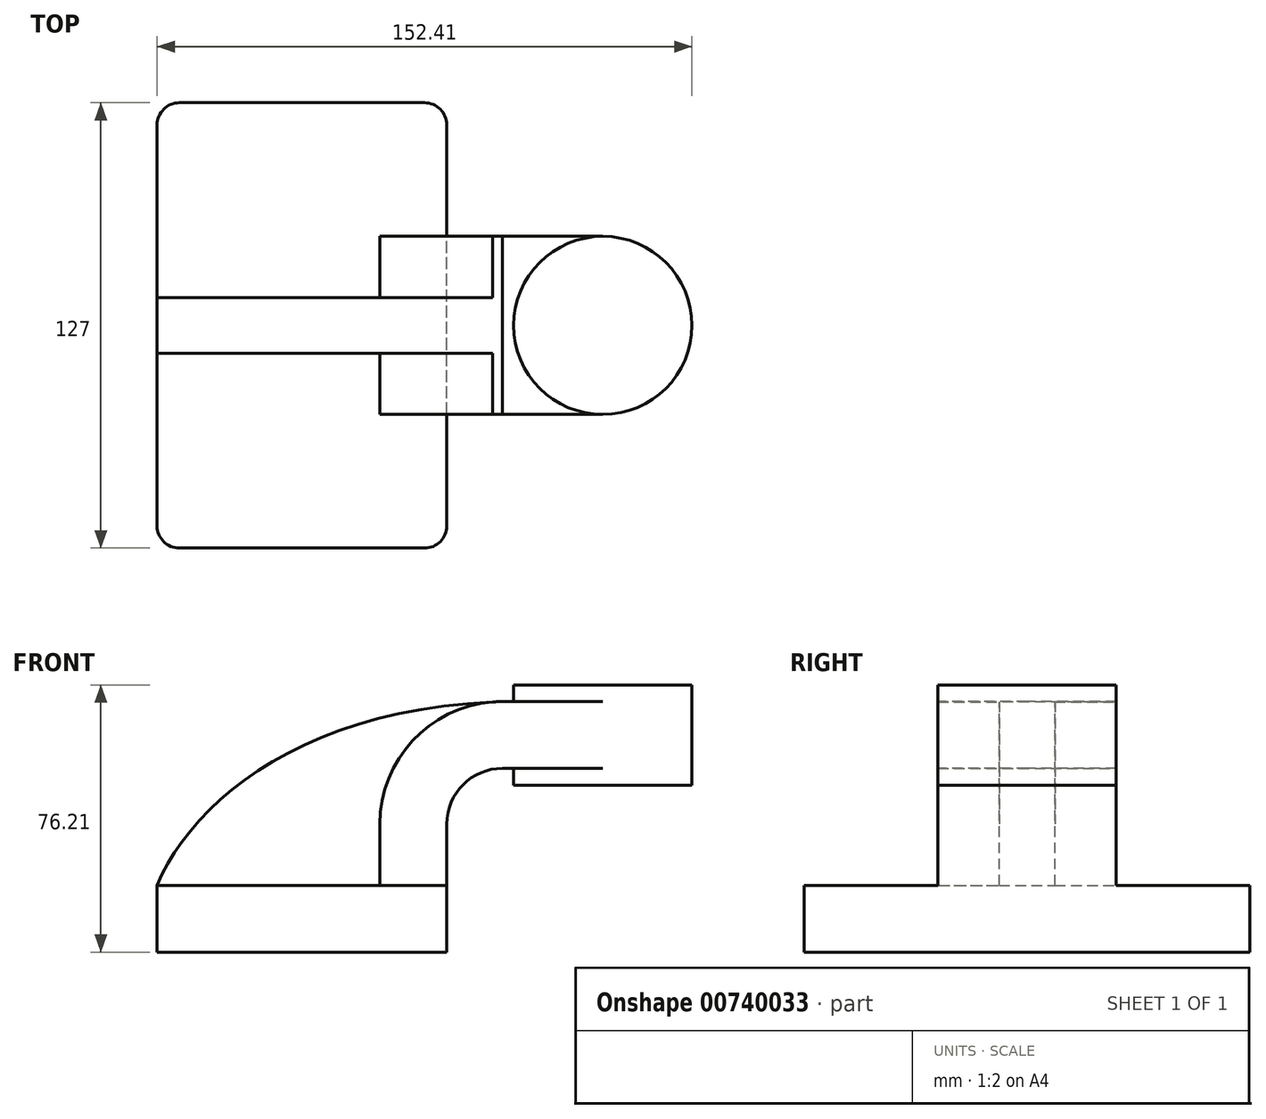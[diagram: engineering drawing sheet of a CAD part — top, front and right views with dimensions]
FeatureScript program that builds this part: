
annotation { "Feature Type Name" : "Feature", "Feature Type Description" : "" }
export const myFeature = defineFeature(function(context is Context, id is Id, definition is map)
    precondition{}
    {
        {
            var Q0;
            Q0=qCreatedBy(makeId("Front.planeOp"),FACE);
            var sketch = newSketch(context, id + "F0", { "sketchPlane" : qUnion([Q0])});
            skLineSegment(sketch, "E0.bottom", {"start": v(-41.28, 9.52) * mm, "end": v(41.28, 9.53) * mm});
            skLineSegment(sketch, "E0.top", {"start": v(-41.28, -9.53) * mm, "end": v(41.28, -9.53) * mm});
            skLineSegment(sketch, "E0.left", {"start": v(-41.28, 9.52) * mm, "end": v(-41.28, -9.53) * mm});
            skLineSegment(sketch, "E0.right", {"start": v(41.28, 9.53) * mm, "end": v(41.28, -9.52) * mm});
            skPoint(sketch, "E0.middle", {"position": v(0, 0) * mm});
            skLineSegment(sketch, "E1.bottom", {"start": v(111.12, 38.1) * mm, "end": v(60.32, 38.1) * mm});
            skLineSegment(sketch, "E1.top", {"start": v(111.13, 66.68) * mm, "end": v(60.33, 66.68) * mm});
            skLineSegment(sketch, "E1.left", {"start": v(111.12, 38.1) * mm, "end": v(111.12, 66.68) * mm});
            skLineSegment(sketch, "E1.right", {"start": v(60.32, 38.1) * mm, "end": v(60.33, 66.68) * mm});
            skPoint(sketch, "E1.middle", {"position": v(85.73, 52.39) * mm});
            skLineSegment(sketch, "E2", {"start": v(41.27, 9.53) * mm, "end": v(41.27, 27) * mm});
            skArc(sketch, "E3", {"start": v(41.27, 27) * mm, "mid": v(45.92, 38.23) * mm, "end": v(57.15, 42.88) * mm});
            skLineSegment(sketch, "E4", {"start": v(57.15, 42.88) * mm, "end": v(85.73, 42.88) * mm});
            skLineSegment(sketch, "E5.0", {"start": v(57.15, 61.93) * mm, "end": v(85.73, 61.93) * mm});
            skArc(sketch, "E5.1", {"start": v(22.22, 27) * mm, "mid": v(32.45, 51.7) * mm, "end": v(57.15, 61.93) * mm});
            skLineSegment(sketch, "E5.2", {"start": v(22.23, 9.53) * mm, "end": v(22.23, 27) * mm});
            skFitSpline(sketch, "E6", {"points": [v(-41.28, 9.52) * mm, v(57.15, 61.93) * mm], "startDerivative": vector(30.51, 72.22) * mm, "endDerivative": vector(171.45, 5.65) * mm});
            skLineSegment(sketch, "E7", {"start": v(85.72, 38.1) * mm, "end": v(85.72, 66.68) * mm});
            skSolve(sketch);
        }
        {
            var Q0;
            Q0=makeQuery(id+"F0.imprint","IMPRINT",FACE,{"disambiguationData":[TD([[makeQuery(id+"F0.imprint","IMPRINT",EDGE,{"derivedFrom":sQuery(id+"F0.wireOp",EDGE,"E0.top")}),1.0]])]});
            extrude(context, id + "F1", {"entities" : qUnion([Q0]), "endBound" : BoundingType.SYMMETRIC, "depth" : 127 * mm, "offsetDistance" : 25.4 * mm});
        }
        {
            var Q0;
            {var subQ6=sQuery(id+"F0.wireOp",EDGE,"E2");Q0=makeQuery(id+"F0.imprint","IMPRINT",FACE,{"disambiguationData":[TD([[makeQuery(id+"F0.imprint","IMPRINT",EDGE,{"derivedFrom":subQ6}),1.0]])]});}
            var Q1;
            {var subQ0=sQuery(id+"F0.wireOp",EDGE,"E4");var subQ1=sQuery(id+"F0.wireOp",EDGE,"E1.right");var subQ2=makeQuery(id+"F0.imprint","INTERSECT",VERTEX,{"derivedFrom":[subQ1,subQ0]});Q1=makeQuery(id+"F0.imprint","IMPRINT",FACE,{"disambiguationData":[TD([[makeQuery(id+"F0.imprint","IMPRINT",EDGE,{"disambiguationData":[TD([[subQ2,-1.0]])],"derivedFrom":subQ1}),-1.0]])]});}
            extrude(context, id + "F2", {"entities" : qUnion([Q0, Q1]), "operationType" : NewBodyOperationType.ADD, "endBound" : BoundingType.SYMMETRIC, "depth" : 50.8 * mm, "offsetDistance" : 25.4 * mm});
        }
        {
            var Q0;
            {var subQ3=sQuery(id+"F0.wireOp",EDGE,"E5.2");Q0=makeQuery(id+"F0.imprint","IMPRINT",FACE,{"disambiguationData":[TD([[makeQuery(id+"F0.imprint","IMPRINT",EDGE,{"derivedFrom":subQ3}),1.0]])]});}
            extrude(context, id + "F3", {"entities" : qUnion([Q0]), "operationType" : NewBodyOperationType.ADD, "endBound" : BoundingType.SYMMETRIC, "depth" : 15.88 * mm, "offsetDistance" : 25.4 * mm});
        }
        {
            var Q0;
            {var subQ4=sQuery(id+"F0.wireOp",EDGE,"E1.left");Q0=makeQuery(id+"F0.imprint","IMPRINT",FACE,{"disambiguationData":[TD([[makeQuery(id+"F0.imprint","IMPRINT",EDGE,{"derivedFrom":subQ4}),1.0]])]});}
            var Q1;
            Q1=sQuery(id+"F0.wireOp",EDGE,"E7");
            revolve(context, id + "F4", {"operationType" : NewBodyOperationType.ADD, "surfaceOperationType" : NewSurfaceOperationType.NEW, "entities" : qUnion([Q0]), "axis" : qUnion([Q1]), "revolveType" : RevolveType.FULL});
        }
        {
            var Q0;
            Q0=makeQuery(id+"F1.opExtrude","CAP_EDGE",EDGE,{"disambiguationData":[OSD([sQuery(id+"F0.wireOp",EDGE,"E0.right")])],"isStart":false});
            var Q1;
            Q1=makeQuery(id+"F1.opExtrude","CAP_EDGE",EDGE,{"disambiguationData":[OSD([sQuery(id+"F0.wireOp",EDGE,"E0.left")])],"isStart":false});
            var Q2;
            Q2=makeQuery(id+"F1.opExtrude","CAP_EDGE",EDGE,{"disambiguationData":[OSD([sQuery(id+"F0.wireOp",EDGE,"E0.right")])],"isStart":true});
            var Q3;
            Q3=makeQuery(id+"F1.opExtrude","CAP_EDGE",EDGE,{"disambiguationData":[OSD([sQuery(id+"F0.wireOp",EDGE,"E0.left")])],"isStart":true});
            fillet(context, id + "F5", {"entities" : qUnion([Q0, Q1, Q2, Q3]), "radius" : 6.35 * mm, "tangentPropagation" : true, "allowEdgeOverflow" : false});
        }
    });
